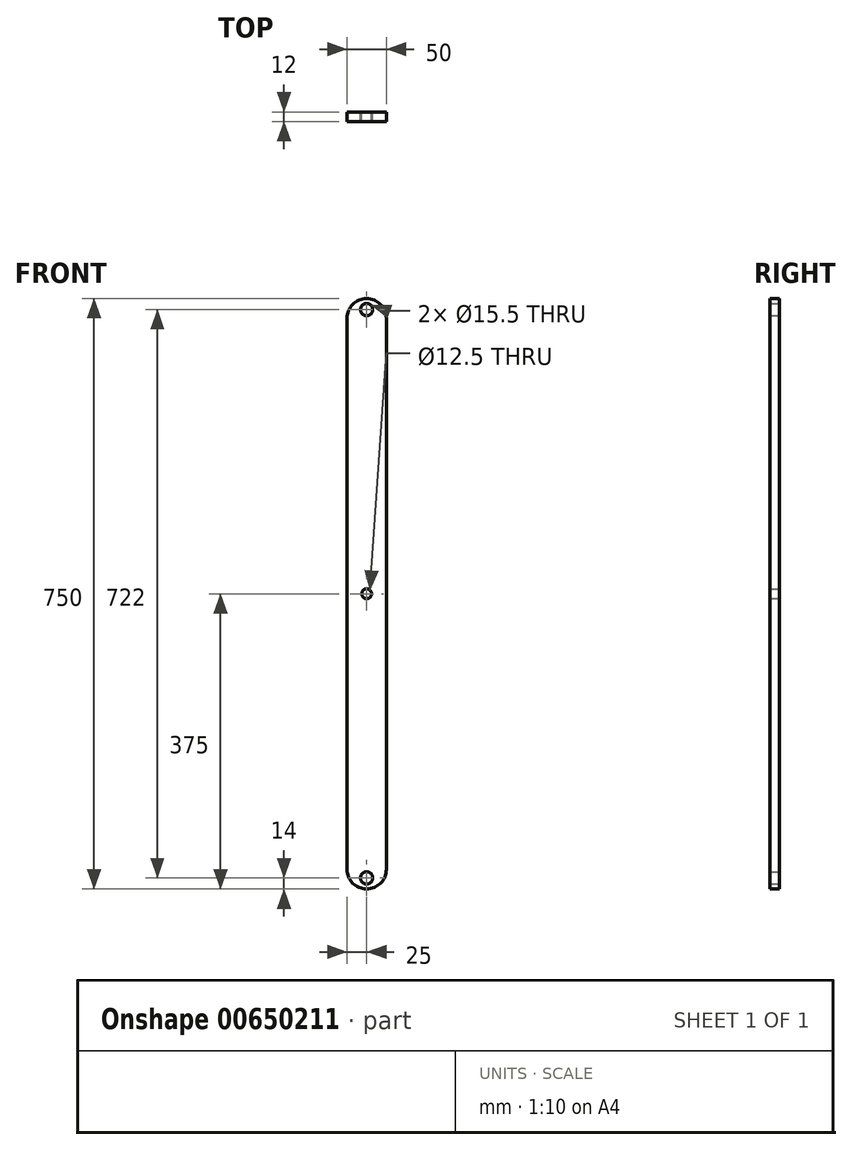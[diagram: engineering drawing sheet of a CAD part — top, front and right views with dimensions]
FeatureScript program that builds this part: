
annotation { "Feature Type Name" : "Feature", "Feature Type Description" : "" }
export const myFeature = defineFeature(function(context is Context, id is Id, definition is map)
    precondition{}
    {
        {
            var Q0;
            Q0=qCreatedBy(makeId("Front.planeOp"),FACE);
            var sketch = newSketch(context, id + "F0", { "sketchPlane" : qUnion([Q0])});
            skLineSegment(sketch, "E0.top", {"start": v(0, -725) * mm, "end": v(50, -725) * mm});
            skLineSegment(sketch, "E0.left", {"start": v(0, -25) * mm, "end": v(0, -725) * mm});
            skLineSegment(sketch, "E0.right", {"start": v(50, -25) * mm, "end": v(50, -725) * mm});
            skCircle(sketch, "E1", {"center": v(25, -14) * mm, "radius": 7.75 * mm});
            skArc(sketch, "E2", {"start": v(25, 0) * mm, "mid": v(7.32, -7.32) * mm, "end": v(0, -25) * mm});
            skArc(sketch, "E3", {"start": v(50, -25) * mm, "mid": v(42.68, -7.32) * mm, "end": v(25, 0) * mm});
            skPoint(sketch, "E4.orphan", {"position": v(0, 0) * mm});
            skPoint(sketch, "E5.orphan", {"position": v(50, 0) * mm});
            skLineSegment(sketch, "E6", {"start": v(50, -375) * mm, "end": v(0, -375) * mm, "construction": true});
            skArc(sketch, "E7.MirrorCS", {"start": v(25, -750) * mm, "mid": v(7.32, -742.68) * mm, "end": v(0, -725) * mm});
            skArc(sketch, "E8.MirrorCS", {"start": v(50, -725) * mm, "mid": v(42.68, -742.68) * mm, "end": v(25, -750) * mm});
            skCircle(sketch, "E9.MirrorC", {"center": v(25, -736) * mm, "radius": 7.75 * mm});
            skCircle(sketch, "E10", {"center": v(25, -375) * mm, "radius": 6.25 * mm});
            skSolve(sketch);
        }
        {
            var Q0;
            Q0=makeQuery(id+"F0.imprint","IMPRINT",FACE,{"disambiguationData":[TD([[makeQuery(id+"F0.imprint","IMPRINT",EDGE,{"derivedFrom":sQuery(id+"F0.wireOp",EDGE,"E0.top")}),1.0]])]});
            var Q1;
            Q1=makeQuery(id+"F0.imprint","IMPRINT",FACE,{"disambiguationData":[TD([[makeQuery(id+"F0.imprint","IMPRINT",EDGE,{"derivedFrom":sQuery(id+"F0.wireOp",EDGE,"E1")}),-1.0]])]});
            var Q2;
            Q2=makeQuery(id+"F0.imprint","IMPRINT",FACE,{"disambiguationData":[TD([[makeQuery(id+"F0.imprint","IMPRINT",EDGE,{"derivedFrom":sQuery(id+"F0.wireOp",EDGE,"E0.top")}),-1.0]])]});
            var Q3;
            Q3=sQuery(id+"F0.wireOp",EDGE,"E3");
            extrude(context, id + "F1", {"entities" : qUnion([Q0, Q1, Q2]), "surfaceEntities" : qUnion([Q3]), "depth" : 12 * mm, "offsetDistance" : 25 * mm});
        }
    });
